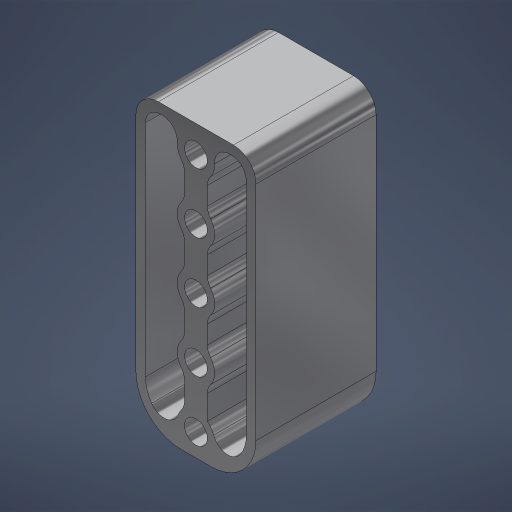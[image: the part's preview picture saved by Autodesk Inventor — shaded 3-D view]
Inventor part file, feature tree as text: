
AUTODESK INVENTOR PART (.ipt)
format: ipt  version: 2024.3 (Build 283343000, 343)  size: 343,040 bytes
history: native  units: mm (DEFAULTED — no unit token found)
features: fillet x3, sketch x3, extrude x2, hole x1, pattern_linear x1, projected_geometry x1
ambient origin geometry x8: Origin, YZ Plane, XZ Plane, XY Plane, X Axis, Y Axis, Z Axis, Center Point
bodies: Solid1 (feature_tree)
feature tree (11):
  extrude  "Extrusion1"  Depth=61.2775mm
  hole  "Hole1"  [1 undecoded]
  fillet  "Fillet1"  Radius=4.7625mm
  pattern_linear  "Rectangular Pattern1"  Count1=5 Spacing1=12.7mm
  extrude  "Extrusion2"  Depth=4.7625mm
  fillet  "Fillet2"  Radius=2.032mm
  fillet  "Fillet3"  [1 undecoded]
  sketch  "Sketch2"  dims[d0=25.4mm d1=61.2775mm]
  sketch  "Sketch3"  dims[d2=25.4mm d3=0.0mm d4=9.525mm d5=4.7625mm]
  sketch  "Sketch4"  dims[d6=4.826mm d7=9.652mm d8=9.779mm d9=1.9558mm d10=14.3117mm d11=13.6144mm d12=20.594885mm d13=50.0mm d15=12.7mm d16=7.9375mm d17=2.032mm d18=0.0mm d19=0.0mm d20=3.175mm d21=4.7625mm]
  projected_geometry  "Projected Loop1"
note: 2 required parameter values undecoded (feature->parameter linkage not recoverable at this tier; creation-order binding heuristic only, values carry confidence <= 0.55)
